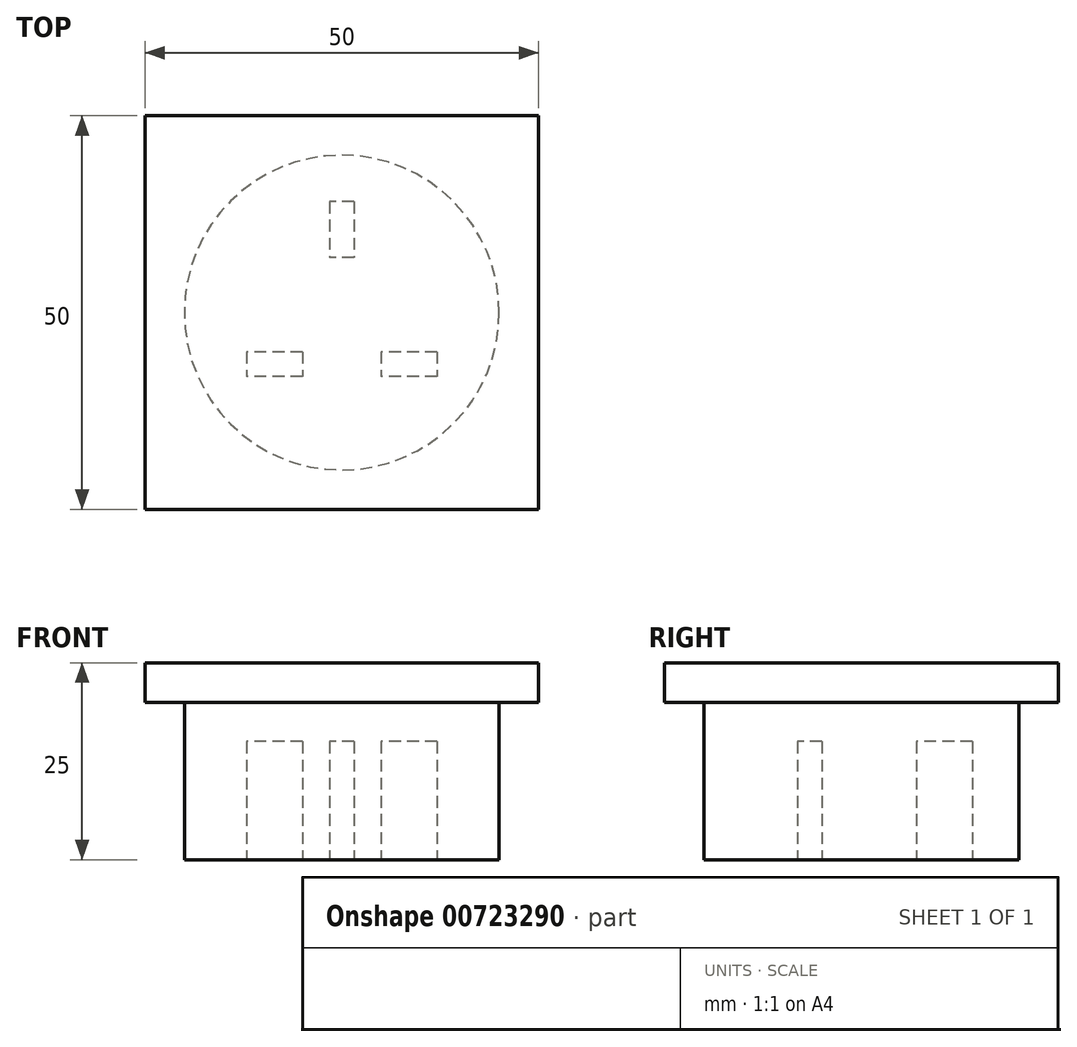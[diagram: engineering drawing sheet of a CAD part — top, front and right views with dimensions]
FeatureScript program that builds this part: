
annotation { "Feature Type Name" : "Feature", "Feature Type Description" : "" }
export const myFeature = defineFeature(function(context is Context, id is Id, definition is map)
    precondition{}
    {
        {
            var Q0;
            Q0=qCreatedBy(makeId("Top.planeOp"),FACE);
            var sketch = newSketch(context, id + "F0", { "sketchPlane" : qUnion([Q0])});
            skCircle(sketch, "E0", {"center": v(0, 0) * mm, "radius": 20 * mm});
            skSolve(sketch);
        }
        {
            var Q0;
            Q0 = qSketchRegion(id + "F0", true);
            extrude(context, id + "F1", {"entities" : qUnion([Q0]), "depth" : 20 * mm, "offsetDistance" : 25 * mm});
        }
        {
            var Q0;
            Q0=makeQuery(id+"F1.opExtrude","CAP_FACE",FACE,{"disambiguationData":[OSD([sQuery(id+"F0.wireOp",EDGE,"E0")])],"isStart":true});
            var sketch = newSketch(context, id + "F2", { "sketchPlane" : qUnion([Q0])});
            skLineSegment(sketch, "E1.bottom", {"start": v(1.55, -14.1) * mm, "end": v(-1.55, -14.1) * mm});
            skLineSegment(sketch, "E1.top", {"start": v(1.55, -7) * mm, "end": v(-1.55, -7) * mm});
            skLineSegment(sketch, "E1.left", {"start": v(1.55, -14.1) * mm, "end": v(1.55, -7) * mm});
            skLineSegment(sketch, "E1.right", {"start": v(-1.55, -14.1) * mm, "end": v(-1.55, -7) * mm});
            skLineSegment(sketch, "E2.bottom", {"start": v(12.1, 5) * mm, "end": v(5, 5) * mm});
            skLineSegment(sketch, "E2.top", {"start": v(12.1, 8.1) * mm, "end": v(5, 8.1) * mm});
            skLineSegment(sketch, "E2.left", {"start": v(12.1, 5) * mm, "end": v(12.1, 8.1) * mm});
            skLineSegment(sketch, "E2.right", {"start": v(5, 5) * mm, "end": v(5, 8.1) * mm});
            skLineSegment(sketch, "E3.bottom", {"start": v(-5, 5) * mm, "end": v(-12.1, 5) * mm});
            skLineSegment(sketch, "E3.top", {"start": v(-5, 8.1) * mm, "end": v(-12.1, 8.1) * mm});
            skLineSegment(sketch, "E3.left", {"start": v(-5, 5) * mm, "end": v(-5, 8.1) * mm});
            skLineSegment(sketch, "E3.right", {"start": v(-12.1, 5) * mm, "end": v(-12.1, 8.1) * mm});
            skSolve(sketch);
        }
        {
            var Q0;
            Q0 = qSketchRegion(id + "F2", true);
            extrude(context, id + "F3", {"entities" : qUnion([Q0]), "operationType" : NewBodyOperationType.REMOVE, "oppositeDirection" : true, "depth" : 15 * mm, "offsetDistance" : 25 * mm});
        }
        {
            var Q0;
            Q0=makeQuery(id+"F1.opExtrude","CAP_FACE",FACE,{"disambiguationData":[OSD([sQuery(id+"F0.wireOp",EDGE,"E0")])],"isStart":false});
            var sketch = newSketch(context, id + "F4", { "sketchPlane" : qUnion([Q0])});
            skLineSegment(sketch, "E4.bottom", {"start": v(-25, -25) * mm, "end": v(25, -25) * mm});
            skLineSegment(sketch, "E4.top", {"start": v(-25, 25) * mm, "end": v(25, 25) * mm});
            skLineSegment(sketch, "E4.left", {"start": v(-25, -25) * mm, "end": v(-25, 25) * mm});
            skLineSegment(sketch, "E4.right", {"start": v(25, -25) * mm, "end": v(25, 25) * mm});
            skSolve(sketch);
        }
        {
            var Q0;
            Q0 = qSketchRegion(id + "F4", true);
            extrude(context, id + "F5", {"entities" : qUnion([Q0]), "operationType" : NewBodyOperationType.ADD, "depth" : 5 * mm, "offsetDistance" : 25 * mm});
        }
    });
